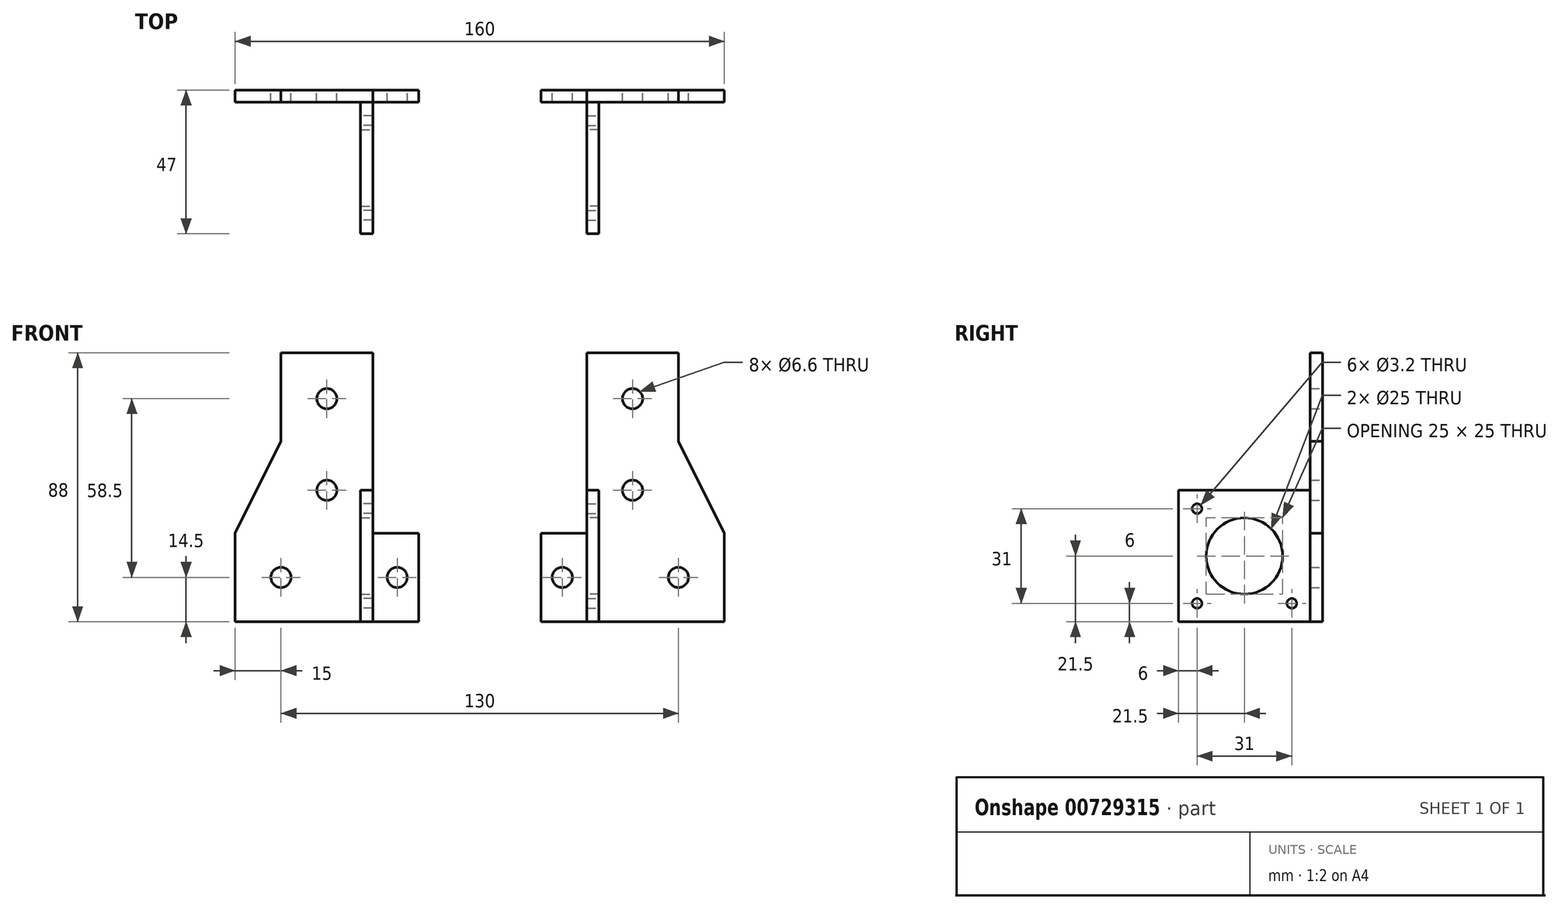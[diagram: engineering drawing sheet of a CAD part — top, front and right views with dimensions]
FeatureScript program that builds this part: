
annotation { "Feature Type Name" : "Feature", "Feature Type Description" : "" }
export const myFeature = defineFeature(function(context is Context, id is Id, definition is map)
    precondition{}
    {
        {
            var Q0;
            Q0=qCreatedBy(makeId("Front.planeOp"),FACE);
            var sketch = newSketch(context, id + "F0", { "sketchPlane" : qUnion([Q0])});
            skLineSegment(sketch, "E0", {"start": v(-30, 0) * mm, "end": v(-30, -29) * mm});
            skLineSegment(sketch, "E1", {"start": v(-30, -29) * mm, "end": v(30, -29) * mm});
            skLineSegment(sketch, "E2", {"start": v(30, -29) * mm, "end": v(30, 0) * mm});
            skLineSegment(sketch, "E3", {"start": v(30, 0) * mm, "end": v(15, 30) * mm});
            skLineSegment(sketch, "E4", {"start": v(15, 30) * mm, "end": v(15, 59) * mm});
            skLineSegment(sketch, "E5", {"start": v(15, 59) * mm, "end": v(-15, 59) * mm});
            skLineSegment(sketch, "E6", {"start": v(-15, 59) * mm, "end": v(-15, 0) * mm});
            skLineSegment(sketch, "E7", {"start": v(-15, 0) * mm, "end": v(-30, 0) * mm});
            skPoint(sketch, "E8", {"position": v(0, 59) * mm});
            skPoint(sketch, "E9", {"position": v(0, -29) * mm});
            skSolve(sketch);
        }
        {
            var Q0;
            Q0=makeQuery(id+"F0.imprint","IMPRINT",FACE,{"disambiguationData":[TD([[makeQuery(id+"F0.imprint","IMPRINT",EDGE,{"derivedFrom":sQuery(id+"F0.wireOp",EDGE,"E0")}),1.0]])]});
            extrude(context, id + "F1", {"entities" : qUnion([Q0]), "depth" : 4 * mm, "offsetDistance" : 25 * mm});
        }
        {
            var Q0;
            Q0=makeQuery(id+"F1.opExtrude","CAP_FACE",FACE,{"disambiguationData":[OSD([sQuery(id+"F0.wireOp",EDGE,"E0"),sQuery(id+"F0.wireOp",EDGE,"E1"),sQuery(id+"F0.wireOp",EDGE,"E2"),sQuery(id+"F0.wireOp",EDGE,"E3"),sQuery(id+"F0.wireOp",EDGE,"E4"),sQuery(id+"F0.wireOp",EDGE,"E5"),sQuery(id+"F0.wireOp",EDGE,"E6"),sQuery(id+"F0.wireOp",EDGE,"E7")])],"isStart":false});
            var sketch = newSketch(context, id + "F2", { "sketchPlane" : qUnion([Q0])});
            skLineSegment(sketch, "E10.bottom", {"start": v(-15, 14) * mm, "end": v(-11, 14) * mm});
            skLineSegment(sketch, "E10.top", {"start": v(-15, -29) * mm, "end": v(-11, -29) * mm});
            skLineSegment(sketch, "E10.left", {"start": v(-15, 14) * mm, "end": v(-15, -29) * mm});
            skLineSegment(sketch, "E10.right", {"start": v(-11, 14) * mm, "end": v(-11, -29) * mm});
            skSolve(sketch);
        }
        {
            var Q0;
            {var subQ2=sQuery(id+"F2.wireOp",EDGE,"E10.bottom");Q0=makeQuery(id+"F2.imprint","IMPRINT",FACE,{"disambiguationData":[TD([[makeQuery(id+"F2.imprint","IMPRINT",EDGE,{"derivedFrom":subQ2}),-1.0]])]});}
            var Q1;
            Q1=sQuery(id+"F2.wireOp",EDGE,"E10.right");
            extrude(context, id + "F3", {"entities" : qUnion([Q0]), "operationType" : NewBodyOperationType.ADD, "surfaceEntities" : qUnion([Q1]), "depth" : 43 * mm, "offsetDistance" : 25 * mm});
        }
        {
            var Q0;
            Q0=makeQuery(id+"F3.boolean.opBoolean","MERGE",FACE,{"derivedFrom":[makeQuery(id+"F1.opExtrude","SWEPT_FACE",FACE,{"disambiguationData":[OSD([sQuery(id+"F0.wireOp",EDGE,"E6")])]}),makeQuery(id+"F3.opExtrude","SWEPT_FACE",FACE,{"disambiguationData":[OSD([sQuery(id+"F2.wireOp",EDGE,"E10.left")])]})]});
            var sketch = newSketch(context, id + "F4", { "sketchPlane" : qUnion([Q0])});
            skCircle(sketch, "E11", {"center": v(25.5, -7.5) * mm, "radius": 12.5 * mm});
            skLineSegment(sketch, "E12.bottom", {"start": v(41, 8) * mm, "end": v(10, 8) * mm, "construction": true});
            skLineSegment(sketch, "E12.top", {"start": v(41, -23) * mm, "end": v(10, -23) * mm, "construction": true});
            skLineSegment(sketch, "E12.left", {"start": v(41, 8) * mm, "end": v(41, -23) * mm, "construction": true});
            skLineSegment(sketch, "E12.right", {"start": v(10, 8) * mm, "end": v(10, -23) * mm, "construction": true});
            skPoint(sketch, "E13", {"position": v(10, 8) * mm});
            skPoint(sketch, "E14", {"position": v(41, 8) * mm});
            skPoint(sketch, "E15", {"position": v(41, -23) * mm});
            skPoint(sketch, "E16", {"position": v(10, -23) * mm});
            skPoint(sketch, "E17", {"position": v(47, -7.5) * mm});
            skPoint(sketch, "E18", {"position": v(25.5, -29) * mm});
            skSolve(sketch);
        }
        {
            var Q0;
            Q0=makeQuery(id+"F4.imprint","IMPRINT",FACE,{"disambiguationData":[TD([[makeQuery(id+"F4.imprint","IMPRINT",EDGE,{"derivedFrom":sQuery(id+"F4.wireOp",EDGE,"E11")}),1.0]])]});
            extrude(context, id + "F5", {"entities" : qUnion([Q0]), "operationType" : NewBodyOperationType.REMOVE, "endBound" : BoundingType.THROUGH_ALL, "oppositeDirection" : true, "depth" : 25 * mm, "offsetDistance" : 25 * mm});
        }
        {
            var Q0;
            Q0=sQuery(id+"F4.wireOp",VERTEX,"E14");
            var Q1;
            Q1=sQuery(id+"F4.wireOp",VERTEX,"E15");
            var Q2;
            Q2=sQuery(id+"F4.wireOp",VERTEX,"E16");
            var Q3;
            Q3=makeQuery(id+"F1.opExtrude","SWEPT_BODY",BODY,{"disambiguationData":[OSD([sQuery(id+"F0.wireOp",EDGE,"E0"),sQuery(id+"F0.wireOp",EDGE,"E1"),sQuery(id+"F0.wireOp",EDGE,"E2"),sQuery(id+"F0.wireOp",EDGE,"E3"),sQuery(id+"F0.wireOp",EDGE,"E4"),sQuery(id+"F0.wireOp",EDGE,"E5"),sQuery(id+"F0.wireOp",EDGE,"E6"),sQuery(id+"F0.wireOp",EDGE,"E7")])]});
            hole(context, id + "F6", {"style" : HoleStyle.SIMPLE, "endStyle" : HoleEndStyle.THROUGH, "standardTappedOrClearance" : lookupTablePath({ "fit" : "Close", "standard" : "ISO", "size" : "M3", "type" : "Clearance" }), "standardBlindInLast" : lookupTablePath({ "fit" : "Close", "standard" : "ISO", "engagement" : "75%", "pitch" : "0.5 mm", "size" : "M3", "type" : "Clearance & tapped" }), "holeDiameter" : 3.2 * mm, "majorDiameter" : 5 * mm, "isTappedThrough" : true, "tappedDepth" : 12 * mm, "tapClearance" : 3, "locations" : qUnion([Q0, Q1, Q2]), "scope" : qUnion([Q3])});
        }
        {
            var Q0;
            {var subQ0=sQuery(id+"F0.wireOp",EDGE,"E4");var subQ1=sQuery(id+"F0.wireOp",EDGE,"E3");var subQ2=sQuery(id+"F0.wireOp",EDGE,"E2");var subQ3=sQuery(id+"F0.wireOp",EDGE,"E1");var subQ4=sQuery(id+"F0.wireOp",EDGE,"E5");var subQ5=sQuery(id+"F0.wireOp",EDGE,"E6");Q0=makeQuery(id+"F3.boolean.opBoolean","SPLIT",FACE,{"disambiguationData":[TD([makeQuery(id+"F1.opExtrude","SWEPT_FACE",FACE,{"disambiguationData":[OSD([subQ2])]})])],"derivedFrom":makeQuery(id+"F1.opExtrude","CAP_FACE",FACE,{"disambiguationData":[OSD([sQuery(id+"F0.wireOp",EDGE,"E0"),subQ3,subQ2,subQ1,subQ0,subQ4,subQ5,sQuery(id+"F0.wireOp",EDGE,"E7")])],"isStart":false})});}
            var sketch = newSketch(context, id + "F7", { "sketchPlane" : qUnion([Q0])});
            skPoint(sketch, "E19", {"position": v(0, 44) * mm});
            skPoint(sketch, "E20", {"position": v(0, 14) * mm});
            skPoint(sketch, "E21", {"position": v(15, -14.5) * mm});
            skPoint(sketch, "E21.positionSnap0", {"position": v(30, -14.5) * mm});
            skPoint(sketch, "E22", {"position": v(-23, -14.5) * mm});
            skSolve(sketch);
        }
        {
            var Q0;
            Q0=sQuery(id+"F7.wireOp",VERTEX,"E19");
            var Q1;
            Q1=sQuery(id+"F7.wireOp",VERTEX,"E21");
            var Q2;
            Q2=sQuery(id+"F7.wireOp",VERTEX,"E22");
            var Q3;
            Q3=sQuery(id+"F7.wireOp",VERTEX,"E20");
            var Q4;
            Q4=makeQuery(id+"F1.opExtrude","SWEPT_BODY",BODY,{"disambiguationData":[OSD([sQuery(id+"F0.wireOp",EDGE,"E0"),sQuery(id+"F0.wireOp",EDGE,"E1"),sQuery(id+"F0.wireOp",EDGE,"E2"),sQuery(id+"F0.wireOp",EDGE,"E3"),sQuery(id+"F0.wireOp",EDGE,"E4"),sQuery(id+"F0.wireOp",EDGE,"E5"),sQuery(id+"F0.wireOp",EDGE,"E6"),sQuery(id+"F0.wireOp",EDGE,"E7")])]});
            hole(context, id + "F8", {"style" : HoleStyle.SIMPLE, "endStyle" : HoleEndStyle.THROUGH, "standardTappedOrClearance" : lookupTablePath({ "fit" : "Normal", "standard" : "ISO", "size" : "M6", "type" : "Clearance" }), "standardBlindInLast" : lookupTablePath({ "fit" : "Normal", "standard" : "ISO", "engagement" : "75%", "pitch" : "1 mm", "size" : "M6", "type" : "Clearance & tapped" }), "holeDiameter" : 6.6 * mm, "majorDiameter" : 5 * mm, "isTappedThrough" : true, "tappedDepth" : 12 * mm, "tapClearance" : 3, "locations" : qUnion([Q0, Q1, Q2, Q3]), "scope" : qUnion([Q4])});
        }
        {
            var Q0;
            Q0=makeQuery(id+"F1.opExtrude","CAP_FACE",FACE,{"disambiguationData":[OSD([sQuery(id+"F0.wireOp",EDGE,"E0"),sQuery(id+"F0.wireOp",EDGE,"E1"),sQuery(id+"F0.wireOp",EDGE,"E2"),sQuery(id+"F0.wireOp",EDGE,"E3"),sQuery(id+"F0.wireOp",EDGE,"E4"),sQuery(id+"F0.wireOp",EDGE,"E5"),sQuery(id+"F0.wireOp",EDGE,"E6"),sQuery(id+"F0.wireOp",EDGE,"E7")])],"isStart":true});
            var sketch = newSketch(context, id + "F9", { "sketchPlane" : qUnion([Q0])});
            skLineSegment(sketch, "E23", {"start": v(-15, -14.5) * mm, "end": v(23, -14.5) * mm, "construction": true});
            skPoint(sketch, "E24", {"position": v(0, -14.5) * mm});
            skSolve(sketch);
        }
        {
            var Q0;
            Q0=qCreatedBy(makeId("Right.planeOp"),FACE);
            cPlane(context, id + "F10", {"entities" : qUnion([Q0]), "cplaneType" : CPlaneType.OFFSET, "offset" : 50 * mm, "oppositeDirection" : true, "width" : 150 * mm, "height" : 150 * mm});
        }
        {
            var Q0;
            Q0=makeQuery(id+"F1.opExtrude","SWEPT_BODY",BODY,{"disambiguationData":[OSD([sQuery(id+"F0.wireOp",EDGE,"E0"),sQuery(id+"F0.wireOp",EDGE,"E1"),sQuery(id+"F0.wireOp",EDGE,"E2"),sQuery(id+"F0.wireOp",EDGE,"E3"),sQuery(id+"F0.wireOp",EDGE,"E4"),sQuery(id+"F0.wireOp",EDGE,"E5"),sQuery(id+"F0.wireOp",EDGE,"E6"),sQuery(id+"F0.wireOp",EDGE,"E7")])]});
            var Q1;
            Q1=qCreatedBy(id+"F10.planeOp",FACE);
            mirror(context, id + "F11", {"entities" : qUnion([Q0]), "mirrorPlane" : qUnion([Q1])});
        }
        {
            var Q0;
            Q0=makeQuery(id+"F11.opPattern","COPY",FACE,{"derivedFrom":makeQuery(id+"F1.opExtrude","CAP_FACE",FACE,{"disambiguationData":[OSD([sQuery(id+"F0.wireOp",EDGE,"E0"),sQuery(id+"F0.wireOp",EDGE,"E1"),sQuery(id+"F0.wireOp",EDGE,"E2"),sQuery(id+"F0.wireOp",EDGE,"E3"),sQuery(id+"F0.wireOp",EDGE,"E4"),sQuery(id+"F0.wireOp",EDGE,"E5"),sQuery(id+"F0.wireOp",EDGE,"E6"),sQuery(id+"F0.wireOp",EDGE,"E7")])],"isStart":true}),"instanceName":"1"});
            var sketch = newSketch(context, id + "F12", { "sketchPlane" : qUnion([Q0])});
            skLineSegment(sketch, "E25", {"start": v(77, -14.5) * mm, "end": v(115, -14.5) * mm, "construction": true});
            skPoint(sketch, "E26", {"position": v(100, 14) * mm});
            skPoint(sketch, "E27", {"position": v(100, -14.5) * mm});
            skSolve(sketch);
        }
    });
